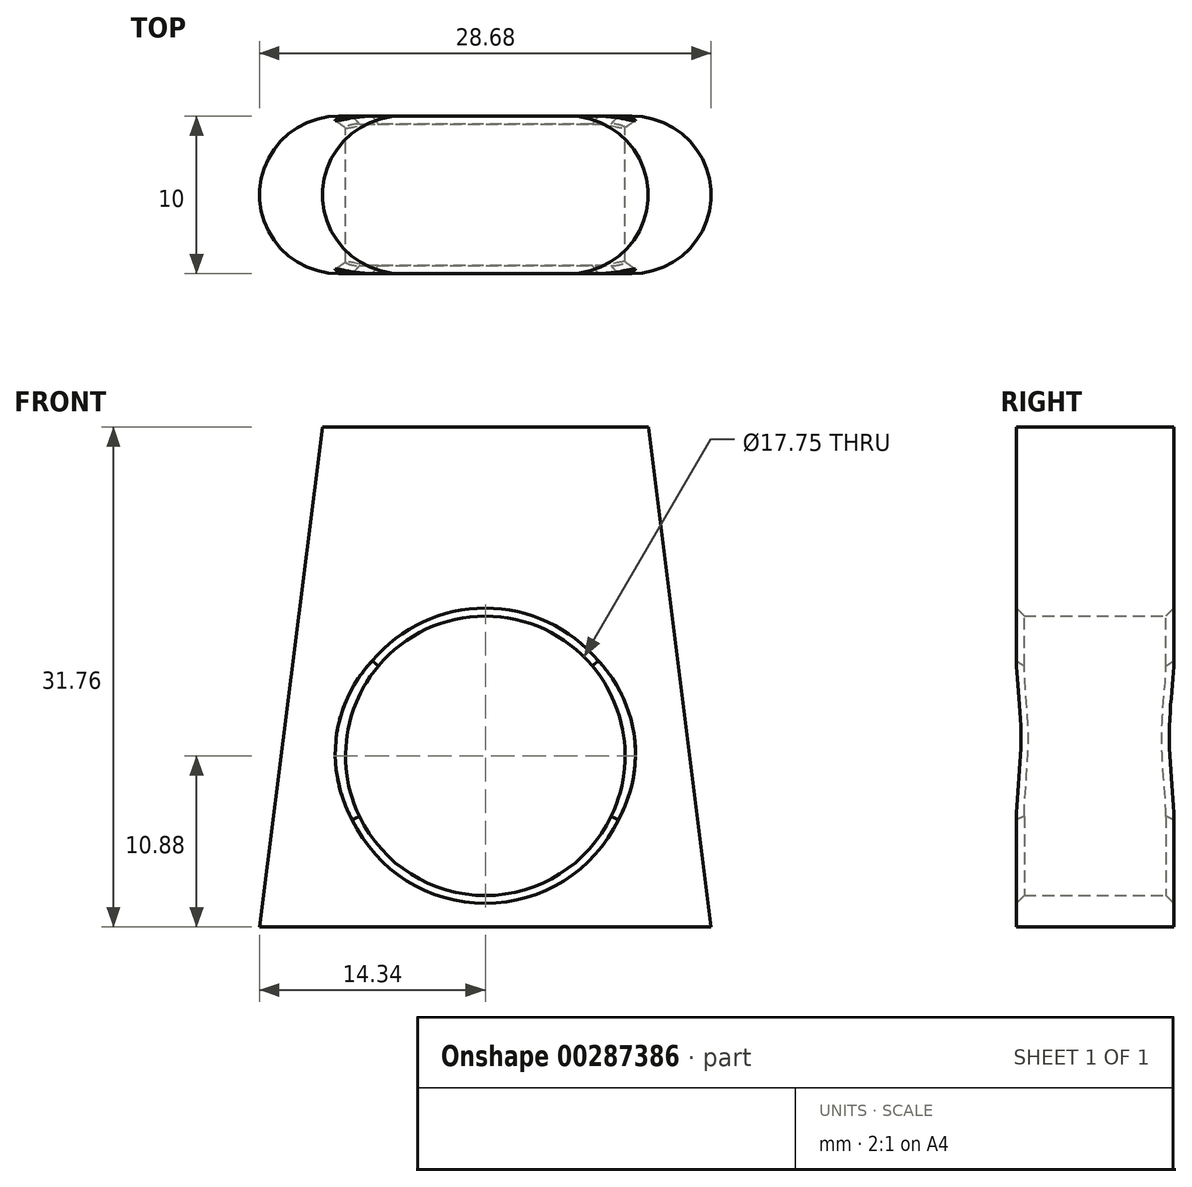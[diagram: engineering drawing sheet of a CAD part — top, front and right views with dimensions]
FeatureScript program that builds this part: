
annotation { "Feature Type Name" : "Feature", "Feature Type Description" : "" }
export const myFeature = defineFeature(function(context is Context, id is Id, definition is map)
    precondition{}
    {
        {
            var Q0;
            Q0=qCreatedBy(makeId("Front.planeOp"),FACE);
            var sketch = newSketch(context, id + "F0", { "sketchPlane" : qUnion([Q0])});
            skCircle(sketch, "E0", {"center": v(0, 0) * mm, "radius": 8.88 * mm});
            skLineSegment(sketch, "E1", {"start": v(-10.35, 20.88) * mm, "end": v(-14.34, -10.88) * mm});
            skLineSegment(sketch, "E2", {"start": v(-14.34, -10.88) * mm, "end": v(0, -10.88) * mm});
            skLineSegment(sketch, "E3", {"start": v(-10.35, 20.88) * mm, "end": v(0, 20.88) * mm});
            skLineSegment(sketch, "E4.MirrorCS", {"start": v(10.35, 20.88) * mm, "end": v(0, 20.88) * mm});
            skLineSegment(sketch, "E5.MirrorCS", {"start": v(10.35, 20.88) * mm, "end": v(14.34, -10.88) * mm});
            skLineSegment(sketch, "E6.MirrorCS", {"start": v(14.34, -10.88) * mm, "end": v(0, -10.88) * mm});
            skSolve(sketch);
        }
        {
            var Q0;
            Q0=makeQuery(id+"F0.imprint","IMPRINT",FACE,{"disambiguationData":[TD([[makeQuery(id+"F0.imprint","IMPRINT",EDGE,{"derivedFrom":sQuery(id+"F0.wireOp",EDGE,"E0")}),-1.0]])]});
            extrude(context, id + "F1", {"entities" : qUnion([Q0]), "depth" : 5 * mm, "hasSecondDirection" : true, "secondDirectionOppositeDirection" : true, "secondDirectionDepth" : 5 * mm});
        }
        {
            var Q0;
            Q0=makeQuery(id+"F1.opExtrude","CAP_EDGE",EDGE,{"disambiguationData":[OSD([sQuery(id+"F0.wireOp",EDGE,"E5.MirrorCS")])],"isStart":false});
            var Q1;
            Q1=makeQuery(id+"F1.opExtrude","CAP_EDGE",EDGE,{"disambiguationData":[OSD([sQuery(id+"F0.wireOp",EDGE,"E5.MirrorCS")])],"isStart":true});
            var Q2;
            Q2=makeQuery(id+"F1.opExtrude","CAP_EDGE",EDGE,{"disambiguationData":[OSD([sQuery(id+"F0.wireOp",EDGE,"E1")])],"isStart":false});
            var Q3;
            Q3=makeQuery(id+"F1.opExtrude","CAP_EDGE",EDGE,{"disambiguationData":[OSD([sQuery(id+"F0.wireOp",EDGE,"E1")])],"isStart":true});
            fillet(context, id + "F2", {"entities" : qUnion([Q0, Q1, Q2, Q3]), "radius" : 5 * mm, "tangentPropagation" : true, "allowEdgeOverflow" : false});
        }
        {
            var Q0;
            Q0=makeQuery(id+"F1.opExtrude","CAP_EDGE",EDGE,{"disambiguationData":[OSD([sQuery(id+"F0.wireOp",EDGE,"E0")])],"isStart":false});
            var Q1;
            Q1=makeQuery(id+"F1.opExtrude","CAP_EDGE",EDGE,{"disambiguationData":[OSD([sQuery(id+"F0.wireOp",EDGE,"E0")])],"isStart":true});
            chamfer(context, id + "F3", {"entities" : qUnion([Q0, Q1]), "width" : .5 * mm, "tangentPropagation" : true});
        }
    });
